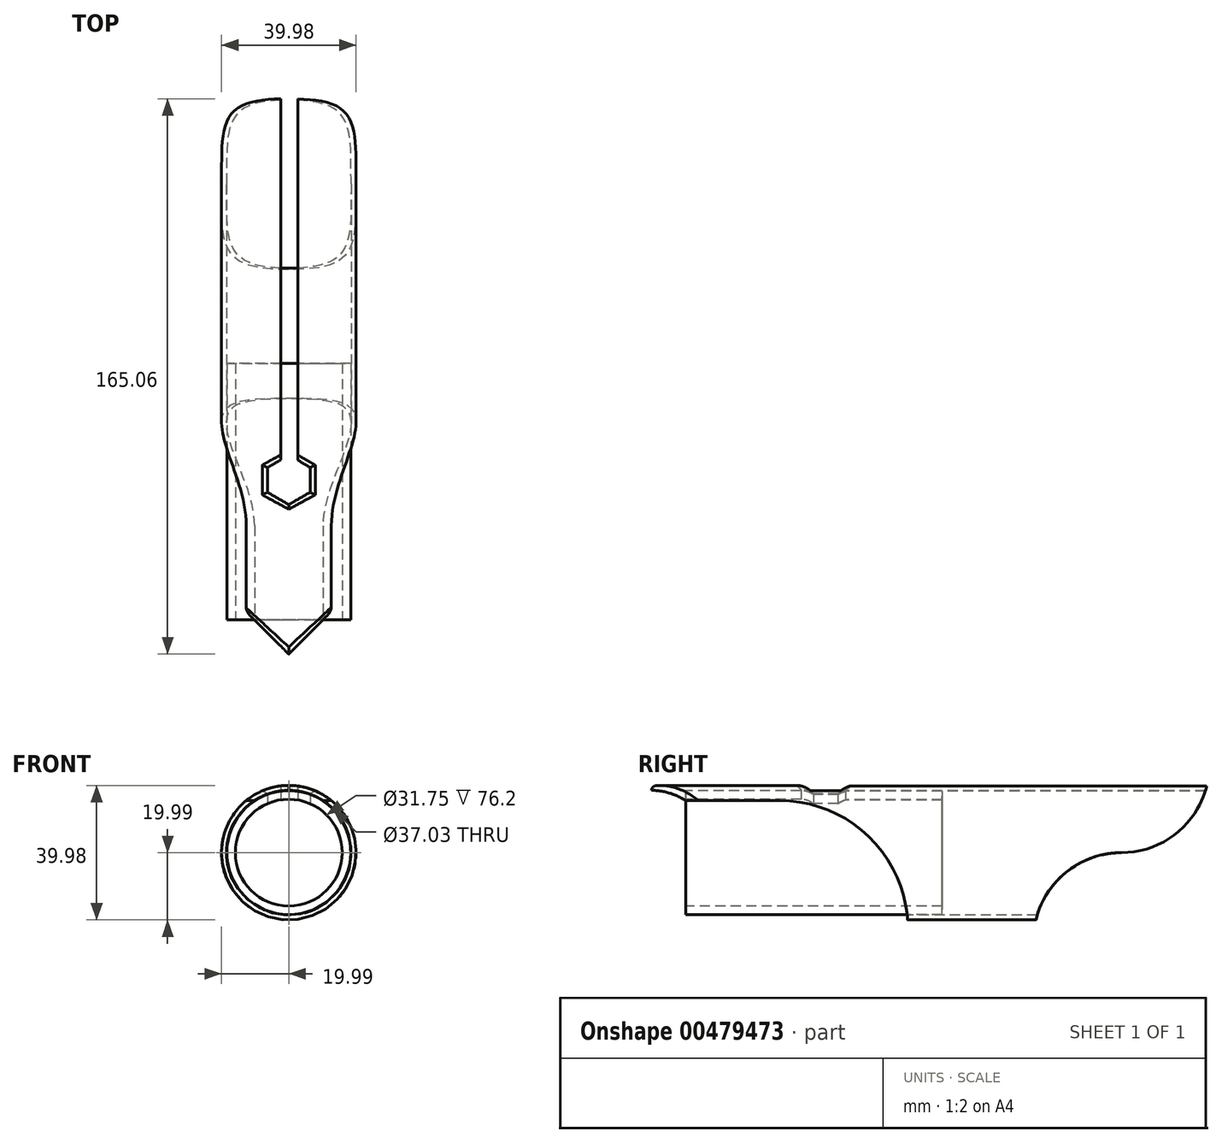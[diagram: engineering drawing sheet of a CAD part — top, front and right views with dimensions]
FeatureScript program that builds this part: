
annotation { "Feature Type Name" : "Feature", "Feature Type Description" : "" }
export const myFeature = defineFeature(function(context is Context, id is Id, definition is map)
    precondition{}
    {
        {
            var Q0;
            Q0=qCreatedBy(makeId("Front.planeOp"),FACE);
            var sketch = newSketch(context, id + "F0", { "sketchPlane" : qUnion([Q0])});
            skCircle(sketch, "E0", {"center": v(0, 0) * mm, "radius": 19.99 * mm});
            skCircle(sketch, "E1", {"center": v(0, 0) * mm, "radius": 18.52 * mm});
            skSolve(sketch);
        }
        {
            var Q0;
            Q0=qSketchRegion(id+"F0",true);
            extrude(context, id + "F1", {"entities" : qUnion([Q0]), "oppositeDirection" : true, "depth" : 165.1 * mm, "offsetDistance" : 25.4 * mm});
        }
        {
            var Q0;
            Q0=qCreatedBy(makeId("Right.planeOp"),FACE);
            var sketch = newSketch(context, id + "F2", { "sketchPlane" : qUnion([Q0])});
            skLineSegment(sketch, "E2", {"start": v(0, -23.5) * mm, "end": v(76.2, -23.57) * mm});
            skLineSegment(sketch, "E3", {"start": v(0, 15.48) * mm, "end": v(0, -23.5) * mm});
            skLineSegment(sketch, "E4", {"start": v(0, 15.48) * mm, "end": v(38.1, 15.48) * mm});
            skArc(sketch, "E5", {"start": v(76.2, -23.57) * mm, "mid": v(65.38, 3.99) * mm, "end": v(38.1, 15.48) * mm});
            skLineSegment(sketch, "E6", {"start": v(165.1, 0) * mm, "end": v(165.1, -20) * mm});
            skLineSegment(sketch, "E7", {"start": v(165.1, -20) * mm, "end": v(114.3, -20) * mm});
            skLineSegment(sketch, "E8", {"start": v(165.1, 0) * mm, "end": v(165.1, 20) * mm});
            skLineSegment(sketch, "E9", {"start": v(165.1, 0) * mm, "end": v(139.7, 0) * mm});
            skArc(sketch, "E10", {"start": v(139.7, 0) * mm, "mid": v(123.54, -5.6) * mm, "end": v(114.3, -20) * mm});
            skArc(sketch, "E11", {"start": v(139.7, 0) * mm, "mid": v(155.86, 5.6) * mm, "end": v(165.1, 20) * mm});
            skSolve(sketch);
        }
        {
            var Q0;
            Q0=qSketchRegion(id+"F2",true);
            extrude(context, id + "F3", {"entities" : qUnion([Q0]), "operationType" : NewBodyOperationType.REMOVE, "endBound" : BoundingType.SYMMETRIC, "oppositeDirection" : true, "depth" : 50.8 * mm, "offsetDistance" : 25.4 * mm});
        }
        {
            var Q0;
            Q0=qCreatedBy(makeId("Top.planeOp"),FACE);
            var sketch = newSketch(context, id + "F4", { "sketchPlane" : qUnion([Q0])});
            skPoint(sketch, "E12.0.midPoint", {"position": v(0, 0) * mm});
            skLineSegment(sketch, "E13", {"start": v(-28.56, 28.44) * mm, "end": v(0, 0) * mm});
            skLineSegment(sketch, "E14", {"start": v(0, 0) * mm, "end": v(28.33, 28.44) * mm});
            skArc(sketch, "E15", {"start": v(28.33, 28.44) * mm, "mid": v(0.08, -40.14) * mm, "end": v(-28.44, 28.33) * mm});
            skSolve(sketch);
        }
        {
            var Q0;
            Q0=qSketchRegion(id+"F4",true);
            extrude(context, id + "F5", {"entities" : qUnion([Q0]), "operationType" : NewBodyOperationType.REMOVE, "depth" : 25.4 * mm, "offsetDistance" : 25.4 * mm});
        }
        {
            var Q0;
            Q0=qCreatedBy(makeId("Front.planeOp"),FACE);
            var sketch = newSketch(context, id + "F6", { "sketchPlane" : qUnion([Q0])});
            skCircle(sketch, "E16", {"center": v(0, 0) * mm, "radius": 18.41 * mm});
            skCircle(sketch, "E17", {"center": v(0, 0) * mm, "radius": 15.88 * mm});
            skSolve(sketch);
        }
        {
            var Q0;
            Q0=qSketchRegion(id+"F6",true);
            extrude(context, id + "F7", {"entities" : qUnion([Q0]), "oppositeDirection" : true, "depth" : 86.36 * mm, "offsetDistance" : 25.4 * mm, "hasSecondDirection" : true, "secondDirectionOppositeDirection" : true, "secondDirectionDepth" : 10.16 * mm});
        }
        {
            var Q0;
            Q0=qCreatedBy(makeId("Top.planeOp"),FACE);
            var sketch = newSketch(context, id + "F8", { "sketchPlane" : qUnion([Q0])});
            skLineSegment(sketch, "E18.0", {"start": v(-6.35, 48.12) * mm, "end": v(-6.35, 55.46) * mm});
            skLineSegment(sketch, "E18.3", {"start": v(6.35, 55.46) * mm, "end": v(6.35, 48.12) * mm});
            skLineSegment(sketch, "E18.4", {"start": v(6.35, 48.12) * mm, "end": v(0, 44.45) * mm});
            skLineSegment(sketch, "E18.5", {"start": v(0, 44.45) * mm, "end": v(-6.35, 48.12) * mm});
            skPoint(sketch, "E18.0.midPoint", {"position": v(-6.35, 51.79) * mm});
            skLineSegment(sketch, "E19", {"start": v(2.65, 57.72) * mm, "end": v(2.65, 180.34) * mm});
            skLineSegment(sketch, "E20", {"start": v(-2.43, 57.72) * mm, "end": v(-2.43, 180.34) * mm});
            skLineSegment(sketch, "E21", {"start": v(-2.43, 180.34) * mm, "end": v(2.65, 180.34) * mm});
            skLineSegment(sketch, "E22", {"start": v(-6.35, 55.46) * mm, "end": v(-2.43, 57.72) * mm});
            skLineSegment(sketch, "E23", {"start": v(2.65, 57.72) * mm, "end": v(6.35, 55.46) * mm});
            skSolve(sketch);
        }
        {
            var Q0;
            Q0=qSketchRegion(id+"F8",true);
            extrude(context, id + "F9", {"entities" : qUnion([Q0]), "operationType" : NewBodyOperationType.REMOVE, "depth" : 25.4 * mm, "offsetDistance" : 25.4 * mm});
        }
        {
            var Q0;
            Q0=makeQuery(id+"F9.boolean.opBoolean","INTERSECT",EDGE,{"derivedFrom":[makeQuery(id+"F1.opExtrude","SWEPT_FACE",FACE,{"disambiguationData":[OSD([sQuery(id+"F0.wireOp",EDGE,"E0")])]}),makeQuery(id+"F9.opExtrude","SWEPT_FACE",FACE,{"disambiguationData":[OSD([sQuery(id+"F8.wireOp",EDGE,"E22")])]})]});
            var Q1;
            Q1=makeQuery(id+"F9.boolean.opBoolean","INTERSECT",EDGE,{"derivedFrom":[makeQuery(id+"F1.opExtrude","SWEPT_FACE",FACE,{"disambiguationData":[OSD([sQuery(id+"F0.wireOp",EDGE,"E0")])]}),makeQuery(id+"F9.opExtrude","SWEPT_FACE",FACE,{"disambiguationData":[OSD([sQuery(id+"F8.wireOp",EDGE,"E23")])]})]});
            var Q2;
            Q2=makeQuery(id+"F9.boolean.opBoolean","INTERSECT",EDGE,{"derivedFrom":[makeQuery(id+"F1.opExtrude","SWEPT_FACE",FACE,{"disambiguationData":[OSD([sQuery(id+"F0.wireOp",EDGE,"E0")])]}),makeQuery(id+"F9.opExtrude","SWEPT_FACE",FACE,{"disambiguationData":[OSD([sQuery(id+"F8.wireOp",EDGE,"E18.4")])]})]});
            var Q3;
            Q3=makeQuery(id+"F9.boolean.opBoolean","INTERSECT",EDGE,{"derivedFrom":[makeQuery(id+"F1.opExtrude","SWEPT_FACE",FACE,{"disambiguationData":[OSD([sQuery(id+"F0.wireOp",EDGE,"E0")])]}),makeQuery(id+"F9.opExtrude","SWEPT_FACE",FACE,{"disambiguationData":[OSD([sQuery(id+"F8.wireOp",EDGE,"E18.5")])]})]});
            chamfer(context, id + "F10", {"entities" : qUnion([Q0, Q1, Q2, Q3]), "chamferType" : ChamferType.TWO_OFFSETS, "width1" : 1.27 * mm, "oppositeDirection" : false, "width2" : 1.27 * mm, "tangentPropagation" : true});
        }
        {
            var Q0;
            Q0=makeQuery(id+"F9.boolean.opBoolean","INTERSECT",EDGE,{"derivedFrom":[makeQuery(id+"F1.opExtrude","SWEPT_FACE",FACE,{"disambiguationData":[OSD([sQuery(id+"F0.wireOp",EDGE,"E0")])]}),makeQuery(id+"F9.opExtrude","SWEPT_FACE",FACE,{"disambiguationData":[OSD([sQuery(id+"F8.wireOp",EDGE,"E18.0")])]})]});
            var Q1;
            Q1=makeQuery(id+"F9.boolean.opBoolean","INTERSECT",EDGE,{"derivedFrom":[makeQuery(id+"F1.opExtrude","SWEPT_FACE",FACE,{"disambiguationData":[OSD([sQuery(id+"F0.wireOp",EDGE,"E0")])]}),makeQuery(id+"F9.opExtrude","SWEPT_FACE",FACE,{"disambiguationData":[OSD([sQuery(id+"F8.wireOp",EDGE,"E18.3")])]})]});
            chamfer(context, id + "F11", {"entities" : qUnion([Q0, Q1]), "chamferType" : ChamferType.TWO_OFFSETS, "width1" : 1.4 * mm, "oppositeDirection" : false, "width2" : 1.52 * mm, "tangentPropagation" : true});
        }
        {
            var Q0;
            Q0=makeQuery(id+"F5.boolean.opBoolean","INTERSECT",EDGE,{"derivedFrom":[makeQuery(id+"F1.opExtrude","SWEPT_FACE",FACE,{"disambiguationData":[OSD([sQuery(id+"F0.wireOp",EDGE,"E0")])]}),makeQuery(id+"F5.opExtrude","SWEPT_FACE",FACE,{"disambiguationData":[OSD([sQuery(id+"F4.wireOp",EDGE,"E13")])]})]});
            var Q1;
            Q1=makeQuery(id+"F5.boolean.opBoolean","INTERSECT",EDGE,{"derivedFrom":[makeQuery(id+"F1.opExtrude","SWEPT_FACE",FACE,{"disambiguationData":[OSD([sQuery(id+"F0.wireOp",EDGE,"E0")])]}),makeQuery(id+"F5.opExtrude","SWEPT_FACE",FACE,{"disambiguationData":[OSD([sQuery(id+"F4.wireOp",EDGE,"E14")])]})]});
            fillet(context, id + "F12", {"entities" : qUnion([Q0, Q1]), "radius" : 1.52 * mm, "tangentPropagation" : true, "rho" : .5, "crossSection" : FilletCrossSection.CONIC, "allowEdgeOverflow" : false});
        }
    });
